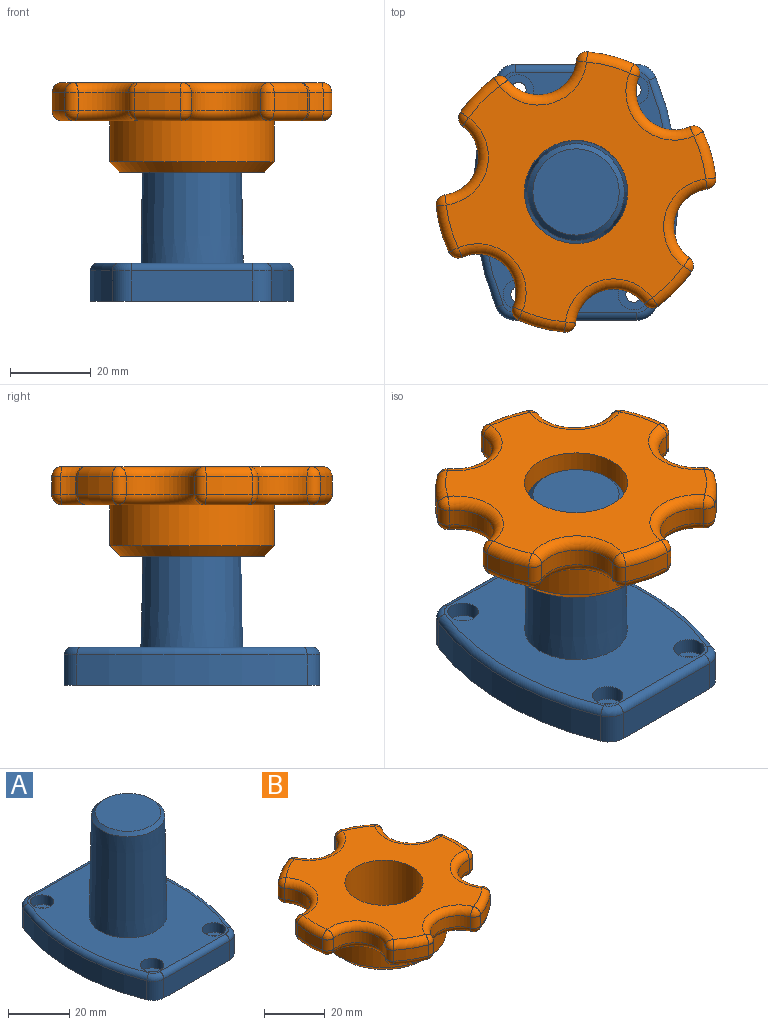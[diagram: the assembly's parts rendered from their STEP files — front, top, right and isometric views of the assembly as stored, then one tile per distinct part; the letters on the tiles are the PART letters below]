
ASSEMBLY  parts=2 mates=1
PART A: 52 faces, bbox 63.4x64.3x50.8 mm
  f0: cone r=12.7mm half-angle=1deg, axis (0,0,-1), area 3105mm2, adj f5,f32
  f1: plane 21.42x21.42mm, normal (0,0,1), area 360.3mm2, adj f32
  f2: plane 30.26x7.62mm, normal (0,-1,0), area 230.6mm2, adj f7,f21,f23,f31
  f3: plane 30.26x7.62mm, normal (0,1,0), area 230.6mm2, adj f7,f20,f22,f24
  f4: cylinder r=76.2mm len=57.15mm, axis (0,0,-1), area 446.4mm2, adj f7,f22,f23,f28
  f5: plane 59.69x46.99mm, normal (0,0,1), area 1867.9mm2, adj f0,f10,f13,f16,f19,f24,f25,f26
  f6: cylinder r=76.2mm len=57.15mm, axis (0,0,-1), area 446.4mm2, adj f7,f20,f21,f27
  f7: plane 63.5x50.8mm, normal (0,0,-1), area 676.7mm2, adj f2,f3,f4,f6,f8,f11,f14,f17
  f8: cylinder r=1.91mm len=5.72mm, axis (0,0,1), area 68.4mm2, adj f7,f9
  f9: plane 7.62x7.62mm, normal (0,0,1), area 34.2mm2, adj f8,f10
  f10: cylinder r=3.81mm len=7.62mm, axis (0,0,1), area 91.2mm2, adj f5,f9
  f11: cylinder r=1.91mm len=5.72mm, axis (0,0,1), area 68.4mm2, adj f7,f12
  f12: plane 7.62x7.62mm, normal (0,0,1), area 34.2mm2, adj f11,f13
  f13: cylinder r=3.81mm len=7.62mm, axis (0,0,1), area 91.2mm2, adj f5,f12
  f14: cylinder r=1.91mm len=5.72mm, axis (0,0,1), area 68.4mm2, adj f7,f15
  f15: plane 7.62x7.62mm, normal (0,0,1), area 34.2mm2, adj f14,f16
  f16: cylinder r=3.81mm len=7.62mm, axis (0,0,1), area 91.2mm2, adj f5,f15
  f17: cylinder r=1.91mm len=5.72mm, axis (0,0,1), area 68.4mm2, adj f7,f18
  f18: plane 7.62x7.62mm, normal (0,0,1), area 34.2mm2, adj f17,f19
  f19: cylinder r=3.81mm len=7.62mm, axis (0,0,1), area 91.2mm2, adj f5,f18
  f20: cylinder r=5.08mm len=7.62mm, axis (0,0,-1), area 45.9mm2, adj f3,f6,f7,f25
  f21: cylinder r=5.08mm len=7.62mm, axis (0,0,-1), area 45.9mm2, adj f2,f6,f7,f29
  f22: cylinder r=5.08mm len=7.62mm, axis (0,0,-1), area 45.9mm2, adj f3,f4,f7,f26
  f23: cylinder r=5.08mm len=7.62mm, axis (0,0,-1), area 45.9mm2, adj f2,f4,f7,f30
  f24: cylinder r=1.91mm len=30.26mm, axis (1,0,0), area 90.5mm2, adj f3,f5,f25,f26
  f25: torus R=3.17mm, axis (0,0,1), area 15.6mm2, adj f5,f20,f24,f27
  f26: torus R=3.17mm, axis (0,0,1), area 15.6mm2, adj f5,f22,f24,f28
  f27: torus R=74.3mm, axis (0,0,1), area 173.7mm2, adj f5,f6,f25,f29
  f28: torus R=74.3mm, axis (0,0,1), area 173.7mm2, adj f4,f5,f26,f30
  f29: torus R=3.17mm, axis (0,0,1), area 15.6mm2, adj f5,f21,f27,f31
  f30: torus R=3.17mm, axis (0,0,1), area 15.6mm2, adj f5,f23,f28,f31
  f31: cylinder r=1.91mm len=30.26mm, axis (-1,0,0), area 90.5mm2, adj f2,f5,f29,f30
  f32: cone r=12mm half-angle=45.5deg, axis (0,0,-1), area 129.3mm2, adj f0,f1
  f33: plane 18.97x18.97mm, normal (0,0,-1), area 282.5mm2, adj f37
  f34: plane 24x6.99mm, normal (0,-1,0), area 146.3mm2, adj f7,f40,f42,f43,f44,f49,f50,f51
  f35: plane 11.61x10.16mm, normal (0,0,-1), area 35.9mm2, adj f38,f41,f47,f48
  f36: plane 11.61x10.16mm, normal (0,0,-1), area 35.9mm2, adj f38,f39,f45,f46
  f37: cone r=10.16mm half-angle=1deg, axis (0,0,-1), area 2553.2mm2, adj f33,f40
  f38: plane 24x6.99mm, normal (0,1,0), area 146.3mm2, adj f7,f35,f36,f40,f45,f46,f47,f48
  f39: cylinder r=73.66mm len=49.09mm, axis (0,0,-1), area 327.9mm2, adj f7,f36,f40,f42,f43,f44,f45,f46
  f40: plane 58.42x45.72mm, normal (0,0,-1), area 1737mm2, adj f34,f37,f38,f39,f41,f44,f46,f48
  f41: cylinder r=73.66mm len=49.09mm, axis (0,0,-1), area 327.9mm2, adj f7,f35,f40,f47,f48,f49,f50,f51
  f42: cylinder r=4.45mm len=8.81mm, axis (0,0,1), area 56.1mm2, adj f7,f34,f39,f43
  f43: plane 11.61x10.16mm, normal (0,0,-1), area 35.9mm2, adj f34,f39,f42,f44
  f44: cylinder r=6.35mm len=11.61mm, axis (0,0,1), area 77.2mm2, adj f34,f39,f40,f43
  f45: cylinder r=4.45mm len=8.81mm, axis (0,0,1), area 56.1mm2, adj f7,f36,f38,f39
  f46: cylinder r=6.35mm len=11.61mm, axis (0,0,1), area 77.2mm2, adj f36,f38,f39,f40
  f47: cylinder r=4.45mm len=8.81mm, axis (0,0,1), area 56.1mm2, adj f7,f35,f38,f41
  f48: cylinder r=6.35mm len=11.61mm, axis (0,0,1), area 77.2mm2, adj f35,f38,f40,f41
  f49: cylinder r=4.45mm len=8.81mm, axis (0,0,1), area 56.1mm2, adj f7,f34,f41,f50
  f50: plane 11.61x10.16mm, normal (0,0,-1), area 35.9mm2, adj f34,f41,f49,f51
  f51: cylinder r=6.35mm len=11.61mm, axis (0,0,1), area 77.2mm2, adj f34,f40,f41,f50
PART B: 78 faces, bbox 70.9x66.5x22.2 mm
  f0: plane 64.77x60.79mm, normal (0,0,1), area 1867.1mm2, adj f8,f30,f33,f34,f37,f38,f41,f42
  f1: cylinder r=34.92mm len=11.89mm, axis (0,0,-1), area 53.1mm2, adj f26,f28,f37,f61
  f2: cylinder r=34.92mm len=10.3mm, axis (0,0,-1), area 53.1mm2, adj f23,f25,f45,f69
  f3: cylinder r=34.92mm len=10.3mm, axis (0,0,-1), area 53.1mm2, adj f20,f22,f53,f77
  f4: cylinder r=34.92mm len=11.89mm, axis (0,0,-1), area 53.1mm2, adj f17,f19,f46,f70
  f5: cylinder r=34.92mm len=10.3mm, axis (0,0,-1), area 53.1mm2, adj f14,f16,f38,f62
  f6: plane 64.77x60.79mm, normal (0,0,-1), area 1070.6mm2, adj f10,f54,f57,f58,f61,f62,f65,f66
  f7: cylinder r=34.92mm len=10.3mm, axis (0,0,-1), area 53.1mm2, adj f13,f29,f30,f54
  f8: cylinder r=12.83mm len=25.65mm, axis (0,0,-1), area 1791.2mm2, adj f0,f9
  f9: plane 35.81x35.81mm, normal (0,0,-1), area 490.5mm2, adj f8,f11
  f10: cylinder r=20.45mm len=40.89mm, axis (0,0,-1), area 1305.3mm2, adj f6,f11
  f11: cone r=17.91mm half-angle=45deg, axis (0,0,1), area 432.8mm2, adj f9,f10
  f12: cylinder r=9.53mm len=17.66mm, axis (0,0,1), area 100.4mm2, adj f13,f14,f34,f58
  f13: cylinder r=2.54mm len=4.45mm, axis (0,0,1), area 17.4mm2, adj f7,f12,f32,f56
  f14: cylinder r=2.54mm len=4.45mm, axis (0,0,-1), area 17.4mm2, adj f5,f12,f36,f60
  f15: cylinder r=9.53mm len=15.38mm, axis (0,0,1), area 100.4mm2, adj f16,f17,f42,f66
  f16: cylinder r=2.54mm len=4.45mm, axis (0,0,1), area 17.4mm2, adj f5,f15,f40,f64
  f17: cylinder r=2.54mm len=4.45mm, axis (0,0,-1), area 17.4mm2, adj f4,f15,f44,f68
  f18: cylinder r=9.53mm len=15.38mm, axis (0,0,1), area 100.4mm2, adj f19,f20,f50,f74
  f19: cylinder r=2.54mm len=4.45mm, axis (0,0,1), area 17.4mm2, adj f4,f18,f48,f72
  f20: cylinder r=2.54mm len=4.45mm, axis (0,0,-1), area 17.4mm2, adj f3,f18,f52,f76
  f21: cylinder r=9.53mm len=17.66mm, axis (0,0,1), area 100.4mm2, adj f22,f23,f49,f73
  f22: cylinder r=2.54mm len=4.45mm, axis (0,0,1), area 17.4mm2, adj f3,f21,f51,f75
  f23: cylinder r=2.54mm len=4.45mm, axis (0,0,-1), area 17.4mm2, adj f2,f21,f47,f71
  f24: cylinder r=9.53mm len=15.38mm, axis (0,0,1), area 100.4mm2, adj f25,f26,f41,f65
  f25: cylinder r=2.54mm len=4.45mm, axis (0,0,1), area 17.4mm2, adj f2,f24,f43,f67
  f26: cylinder r=2.54mm len=4.45mm, axis (0,0,-1), area 17.4mm2, adj f1,f24,f39,f63
  f27: cylinder r=9.53mm len=15.38mm, axis (0,0,1), area 100.4mm2, adj f28,f29,f33,f57
  f28: cylinder r=2.54mm len=4.45mm, axis (0,0,1), area 17.4mm2, adj f1,f27,f35,f59
  f29: cylinder r=2.54mm len=4.45mm, axis (0,0,-1), area 17.4mm2, adj f7,f27,f31,f55
  f30: torus R=32.38mm, axis (0,0,-1), area 46.4mm2, adj f0,f7,f31,f32
  f31: sphere r=2.54mm, area 9.9mm2, adj f29,f30,f33
  f32: sphere r=2.54mm, area 9.9mm2, adj f13,f30,f34
  f33: torus R=12.06mm, axis (0,0,-1), area 98.9mm2, adj f0,f27,f31,f35
  f34: torus R=12.06mm, axis (0,0,-1), area 98.9mm2, adj f0,f12,f32,f36
  f35: sphere r=2.54mm, area 9.9mm2, adj f28,f33,f37
  f36: sphere r=2.54mm, area 9.9mm2, adj f14,f34,f38
  f37: torus R=32.38mm, axis (0,0,-1), area 46.4mm2, adj f0,f1,f35,f39
  f38: torus R=32.38mm, axis (0,0,-1), area 46.4mm2, adj f0,f5,f36,f40
  f39: sphere r=2.54mm, area 9.9mm2, adj f26,f37,f41
  f40: sphere r=2.54mm, area 9.9mm2, adj f16,f38,f42
  f41: torus R=12.06mm, axis (0,0,-1), area 98.9mm2, adj f0,f24,f39,f43
  f42: torus R=12.06mm, axis (0,0,-1), area 98.9mm2, adj f0,f15,f40,f44
  f43: sphere r=2.54mm, area 9.9mm2, adj f25,f41,f45
  f44: sphere r=2.54mm, area 9.9mm2, adj f17,f42,f46
  f45: torus R=32.38mm, axis (0,0,-1), area 46.4mm2, adj f0,f2,f43,f47
  f46: torus R=32.38mm, axis (0,0,-1), area 46.4mm2, adj f0,f4,f44,f48
  f47: sphere r=2.54mm, area 9.9mm2, adj f23,f45,f49
  f48: sphere r=2.54mm, area 9.9mm2, adj f19,f46,f50
  f49: torus R=12.06mm, axis (0,0,-1), area 98.9mm2, adj f0,f21,f47,f51
  f50: torus R=12.06mm, axis (0,0,-1), area 98.9mm2, adj f0,f18,f48,f52
  f51: sphere r=2.54mm, area 9.9mm2, adj f22,f49,f53
  f52: sphere r=2.54mm, area 9.9mm2, adj f20,f50,f53
  f53: torus R=32.38mm, axis (0,0,-1), area 46.4mm2, adj f0,f3,f51,f52
  f54: torus R=32.38mm, axis (0,0,-1), area 46.4mm2, adj f6,f7,f55,f56
  f55: sphere r=2.54mm, area 9.9mm2, adj f29,f54,f57
  f56: sphere r=2.54mm, area 9.9mm2, adj f13,f54,f58
  f57: torus R=12.06mm, axis (0,0,-1), area 98.9mm2, adj f6,f27,f55,f59
  f58: torus R=12.06mm, axis (0,0,-1), area 98.9mm2, adj f6,f12,f56,f60
  f59: sphere r=2.54mm, area 9.9mm2, adj f28,f57,f61
  f60: sphere r=2.54mm, area 9.9mm2, adj f14,f58,f62
  f61: torus R=32.38mm, axis (0,0,-1), area 46.4mm2, adj f1,f6,f59,f63
  f62: torus R=32.38mm, axis (0,0,-1), area 46.4mm2, adj f5,f6,f60,f64
  f63: sphere r=2.54mm, area 9.9mm2, adj f26,f61,f65
  f64: sphere r=2.54mm, area 9.9mm2, adj f16,f62,f66
  f65: torus R=12.06mm, axis (0,0,-1), area 98.9mm2, adj f6,f24,f63,f67
  f66: torus R=12.06mm, axis (0,0,-1), area 98.9mm2, adj f6,f15,f64,f68
  f67: sphere r=2.54mm, area 9.9mm2, adj f25,f65,f69
  f68: sphere r=2.54mm, area 9.9mm2, adj f17,f66,f70
  f69: torus R=32.38mm, axis (0,0,-1), area 46.4mm2, adj f2,f6,f67,f71
  f70: torus R=32.38mm, axis (0,0,-1), area 46.4mm2, adj f4,f6,f68,f72
  f71: sphere r=2.54mm, area 9.9mm2, adj f23,f69,f73
  f72: sphere r=2.54mm, area 9.9mm2, adj f19,f70,f74
  f73: torus R=12.06mm, axis (0,0,-1), area 98.9mm2, adj f6,f21,f71,f75
  f74: torus R=12.06mm, axis (0,0,-1), area 98.9mm2, adj f6,f18,f72,f76
  f75: sphere r=2.54mm, area 9.9mm2, adj f22,f73,f77
  f76: sphere r=2.54mm, area 9.9mm2, adj f20,f74,f77
  f77: torus R=32.38mm, axis (0,0,-1), area 46.4mm2, adj f3,f6,f75,f76
PLACE A t=(-3.61,11.93,-4.37)mm fixed
PLACE B rot(axis=(0,0,-1),164.4deg) t=(-3.61,11.93,27.78)mm
MATE cylindrical A.f0 <-> B.f1  axis (0,0,1) through (-3.61,11.93,46.43)mm
